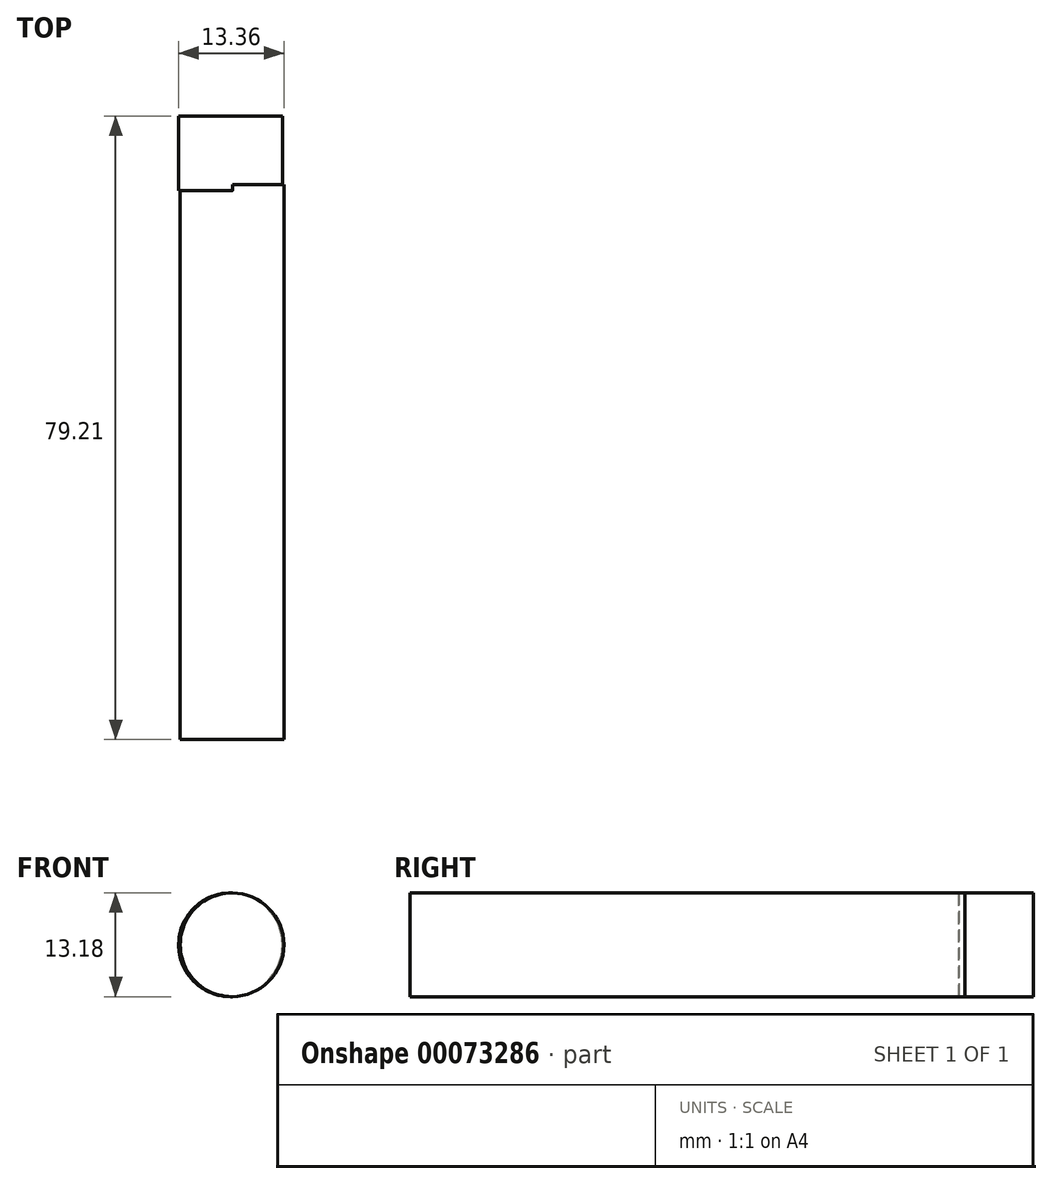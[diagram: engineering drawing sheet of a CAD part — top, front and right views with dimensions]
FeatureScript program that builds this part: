
annotation { "Feature Type Name" : "Feature", "Feature Type Description" : "" }
export const myFeature = defineFeature(function(context is Context, id is Id, definition is map)
    precondition{}
    {
        {
            var Q0;
            Q0=qCreatedBy(makeId("Top.planeOp"),FACE);
            var sketch = newSketch(context, id + "F0", { "sketchPlane" : qUnion([Q0])});
            skLineSegment(sketch, "E0", {"start": v(3.22, 12.93) * mm, "end": v(3.22, 22.17) * mm});
            skLineSegment(sketch, "E1", {"start": v(3.22, 22.17) * mm, "end": v(9.8, 22.17) * mm});
            skLineSegment(sketch, "E2", {"start": v(9.8, 22.17) * mm, "end": v(9.8, 12.67) * mm});
            skLineSegment(sketch, "E3.bottom", {"start": v(3.22, 12.93) * mm, "end": v(9.8, 12.67) * mm});
            skLineSegment(sketch, "E3.right", {"start": v(9.8, 12.67) * mm, "end": v(9.8, 12.67) * mm});
            skPoint(sketch, "E4.end.orphan", {"position": v(6.51, 12.8) * mm});
            skPoint(sketch, "E4.start.orphan", {"position": v(6.51, 22.17) * mm});
            skSolve(sketch);
        }
        {
            var Q0;
            Q0 = qSketchRegion(id + "F0", true);
            var Q1;
            Q1=sQuery(id+"F0.wireOp",EDGE,"E0");
            revolve(context, id + "F1", {"entities" : qUnion([Q0]), "axis" : qUnion([Q1]), "revolveType" : RevolveType.FULL});
        }
        {
            var Q0;
            Q0=qCreatedBy(makeId("Front.planeOp"),FACE);
            var sketch = newSketch(context, id + "F2", { "sketchPlane" : qUnion([Q0])});
            skCircle(sketch, "E5", {"center": v(3.4, 0) * mm, "radius": 6.59 * mm});
            skSolve(sketch);
        }
        {
            var Q0;
            Q0 = qSketchRegion(id + "F2", true);
            extrude(context, id + "F3", {"entities" : qUnion([Q0]), "operationType" : NewBodyOperationType.ADD, "depth" : 57.04 * mm, "hasSecondDirection" : true, "secondDirectionOppositeDirection" : true, "secondDirectionDepth" : 13.45 * mm});
        }
    });
